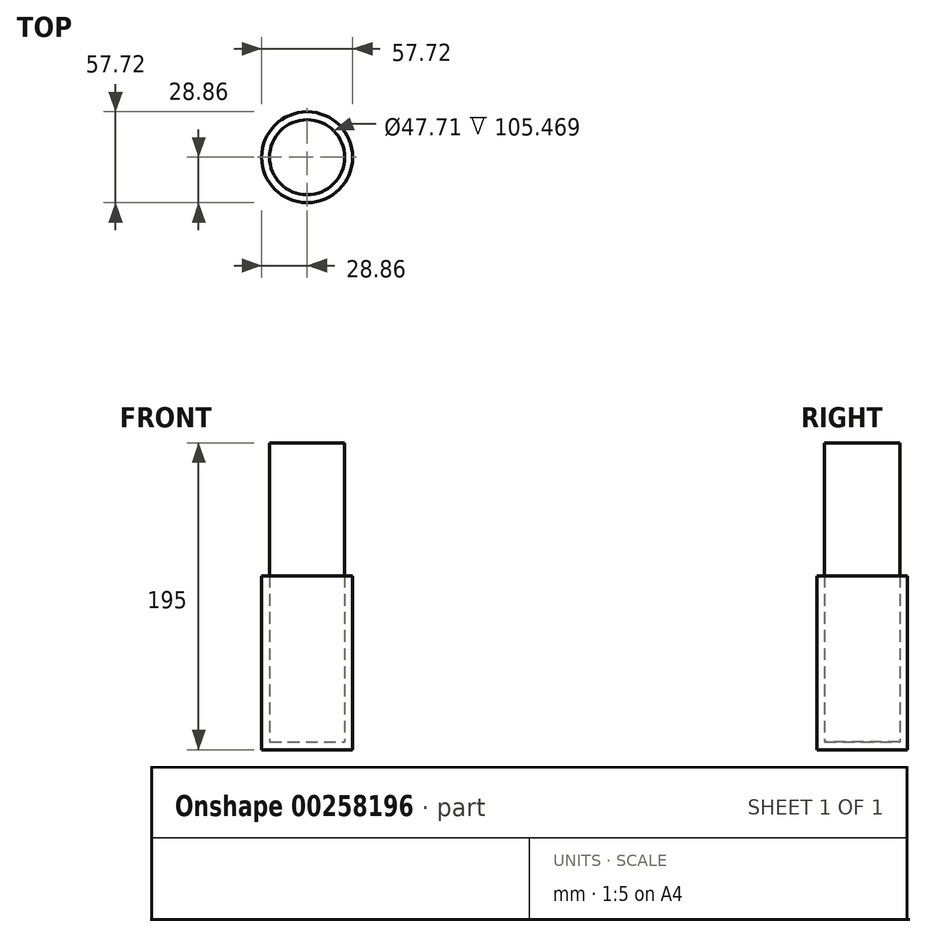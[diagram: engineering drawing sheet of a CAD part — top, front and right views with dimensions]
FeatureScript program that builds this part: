
annotation { "Feature Type Name" : "Feature", "Feature Type Description" : "" }
export const myFeature = defineFeature(function(context is Context, id is Id, definition is map)
    precondition{}
    {
        {
            var Q0;
            Q0=qCreatedBy(makeId("Front.planeOp"),FACE);
            var sketch = newSketch(context, id + "F0", { "sketchPlane" : qUnion([Q0])});
            skLineSegment(sketch, "E0.bottom", {"start": v(-28.86, 55.23) * mm, "end": v(28.86, 55.23) * mm});
            skLineSegment(sketch, "E0.top", {"start": v(-28.86, -55.23) * mm, "end": v(28.86, -55.23) * mm});
            skLineSegment(sketch, "E0.left", {"start": v(-28.86, 55.23) * mm, "end": v(-28.86, -55.23) * mm});
            skLineSegment(sketch, "E0.right", {"start": v(28.86, 55.23) * mm, "end": v(28.86, -55.23) * mm});
            skPoint(sketch, "E0.middle", {"position": v(0, 0) * mm});
            skLineSegment(sketch, "E1", {"start": v(0, 55.23) * mm, "end": v(0, -55.23) * mm});
            skSolve(sketch);
        }
        {
            var Q0;
            {var subQ0=sQuery(id+"F0.wireOp",EDGE,"E0.left");Q0=makeQuery(id+"F0.imprint","IMPRINT",FACE,{"disambiguationData":[TD([[makeQuery(id+"F0.imprint","IMPRINT",EDGE,{"derivedFrom":subQ0}),1.0]])]});}
            var Q1;
            Q1=sQuery(id+"F0.wireOp",EDGE,"E1");
            revolve(context, id + "F1", {"entities" : qUnion([Q0]), "axis" : qUnion([Q1]), "revolveType" : RevolveType.FULL});
        }
        {
            var Q0;
            Q0=makeQuery(id+"F1.opRevolve","SWEPT_FACE",FACE,{"disambiguationData":[OSD([sQuery(id+"F0.wireOp",EDGE,"E0.bottom")])]});
            shell(context, id + "F2", {"entities" : qUnion([Q0]), "thickness" : 5 * mm});
        }
        {
            var Q0;
            Q0=makeQuery(id+"F2.opShell","OFFSET_FACE",FACE,{"disambiguationData":[OSD([sQuery(id+"F0.wireOp",EDGE,"E0.top")])]});
            extrude(context, id + "F3", {"entities" : qUnion([Q0]), "depth" : 190 * mm});
        }
    });
